# Revit family: ef_eg-40_60dra2_era2_fra2_60Hz
name_source: partatom
category: 機械設備
units: mm (PartAtom-declared; Revit-internal decimal feet)

## family parameters
OmniClass タイトル = Industrial Ventilating Equipment
OmniClass 番号 = 23.75.35.21.17
パーツ タイプ = 標準
ロード時にボイドで切り取り = はい
丸型コネクタ寸法 = 直径を使用
作業面ベース = いいえ
共有 = いいえ
常に垂直 = はい
部屋計算ポイント = はい

## types (3) — shared parameters
IfcExportAs = IfcFanType
IfcExportType = TUBEAXIAL
MID風量 = 0.0 m³/h
MIN風量 = 0.0 m³/h
OmniClassCode = 23-33 31 19 11 17
URL = https://www.mitsubishielectric.co.jp
Uniclass2015Code = Pr_65_67_29_67
Uniclass2015Title = Propeller fans
Uniclass2015Version = Systems v1.9
ファンの種類 = 軸流羽根
フレームの厚さ = 10  [stored 0.0328084 ft]
仕様書バージョン = Version1.0
企業コード = 108420
分類コード = 50052503100110
周波数 = 60 Hz
呼称 = 有圧扇
極数 = 3
法定耐用年数 = 15
相 = 3
製品リリース年月 = 2022年6月1日
製品出荷対象 = 国内
製造元 = 三菱電機株式会社
設置方法 = 壁付
説明 = 産業用有圧換気扇 低騒音形 冷凍室タイプ
負荷分類 = 3_ファン類
運転質量 = 0.00 kg
電圧 = 200 V

## per-type parameters (varying)
| type | Depth | Height | MAX風量 | Width | オリフィス_Depth | オリフィス径 | モーター径 | レグ_Depth | レグ_Height | レグ_Width | 価格 | 極 | 消費電力 | 羽根径 | 製品質量 | 質量 | 電動機出力 |
| EF-40DRA2 | 226  [stored 0.74147 ft] | 520  [stored 1.70604 ft] | 3900.0 m³/h | 520  [stored 1.70604 ft] | 80  [stored 0.262467 ft] | 490  [stored 1.60761 ft] | 131  [stored 0.42979 ft] | 199  [stored 0.652887 ft] | 400  [stored 1.31234 ft] | 400  [stored 1.31234 ft] | 150000 $ | 4 | 160 W | ∅400 | 12.50 kg | 15.00 kg | 200 W |
| EF-50ERA2 | 256 | 620  [stored 2.03412 ft] | 6800.0 m³/h | 620  [stored 2.03412 ft] | 95 | 605  [stored 1.98491 ft] | 131  [stored 0.42979 ft] | 231  [stored 0.757874 ft] | 502  [stored 1.64698 ft] | 502  [stored 1.64698 ft] | 195000 $ | 4 | 400 W | ∅500 | 18.00 kg | 21.60 kg | 400 W |
| EG-60FRA2 | 318  [stored 1.04331 ft] | 710 | 10800.0 m³/h | 710 | 100  [stored 0.328084 ft] | 705  [stored 2.31299 ft] | 163  [stored 0.534777 ft] | 282 | 598 | 598 | 260000 $ | 6 | 560 W | ∅600 | 27.30 kg | 32.76 kg | 750 W |

note: column(s) folded — value = type name in every type: モデル

note: [stored X ft] marks values corroborated as IEEE doubles in the binary element streams (Revit-internal decimal feet)
